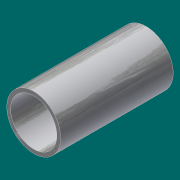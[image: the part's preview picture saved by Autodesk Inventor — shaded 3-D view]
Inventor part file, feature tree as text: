
AUTODESK INVENTOR PART (.ipt)
format: ipt  version: 2017 (Build 210142000, 142)  size: 92,672 bytes
history: native  units: in
note: dims shown in document units (in); Inventor stores cm internally (conversion verified against a paired STEP export)
features: extrude x1, sketch x1
ambient origin geometry x8: Origin, YZ Plane, XZ Plane, XY Plane, X Axis, Y Axis, Z Axis, Center Point
bodies: Solid1 (feature_tree)
feature tree (2):
  extrude  "Extrusion1"  Depth=6.0in
  sketch  "Sketch1"  dims[d0=2.875in d1=2.469in d2=6.0in d3=0.0in]
